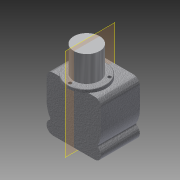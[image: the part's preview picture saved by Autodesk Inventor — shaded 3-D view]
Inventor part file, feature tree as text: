
AUTODESK INVENTOR PART (.ipt)
format: ipt  version: 2018 (Build 220112000, 112)  size: 165,888 bytes
history: native  units: in
note: dims shown in document units (in); Inventor stores cm internally (conversion verified against a paired STEP export)
features: sketch x5, extrude x4, fillet x3, reference x3, projected_geometry x2, hole x1
ambient origin geometry x8: Origin, YZ Plane, XZ Plane, XY Plane, X Axis, Y Axis, Z Axis, Center Point
bodies: Solid1 (feature_tree)
feature tree (18):
  extrude  "Extrusion1"  Depth=2.11in
  fillet  "Fillet1"  Radius=1.5in
  extrude  "Extrusion2"  Depth=0.5in
  fillet  "Fillet2"  Radius=0.5in
  extrude  "Extrusion3"  Depth=1.055in
  fillet  "Fillet3"  Radius=1.0in
  extrude  "Extrusion4"  Depth=1.5in
  hole  "Hole1"  [1 undecoded]
  sketch  "Sketch1"  dims[d0=2.11in d1=2.11in d2=1.5in d3=0.0in]
  sketch  "Sketch3"  dims[d4=0.25in d8=2.0in d9=0.5in]
  sketch  "Sketch4"  dims[d10=0.5in d12=1.055in d13=1.0in d14=0.0in]
  projected_geometry  "Projected Loop1"
  projected_geometry  "Projected Loop2"
  sketch  "Sketch5"  dims[d15=0.0625in d16=1.5in]
  sketch  "Sketch6"  dims[d17=0.25in d18=0.125in d19=0.0in d20=0.0312in d22=1.0in d23=0.0in d24=0.25in d25=0.129in d26=0.75in d27=0.225in d28=0.25in d29=0.5635in d30=0.25in d31=0.8108in]
  reference  "Reference1"
  reference  "Reference2"
  reference  "Reference3"
note: 1 required parameter value undecoded (feature->parameter linkage not recoverable at this tier; creation-order binding heuristic only, values carry confidence <= 0.55)
